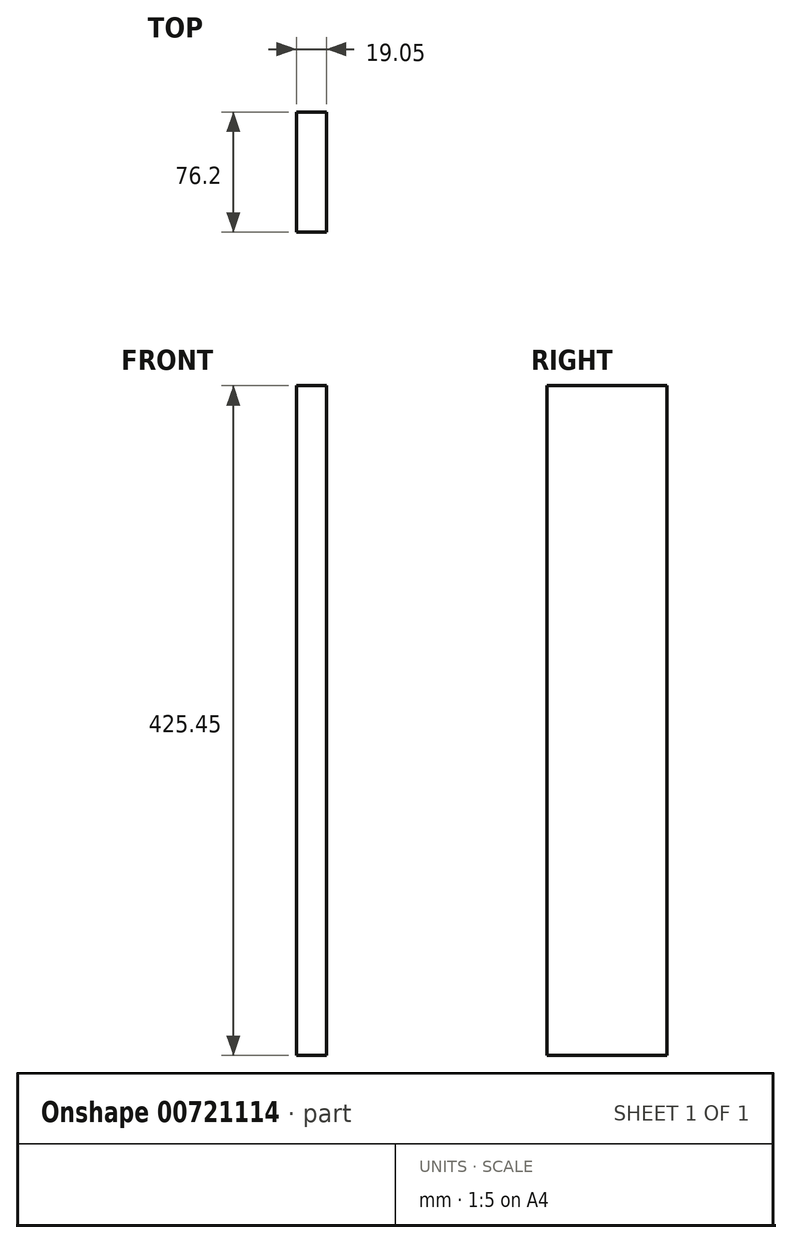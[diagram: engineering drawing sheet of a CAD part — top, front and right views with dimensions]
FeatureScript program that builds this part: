
annotation { "Feature Type Name" : "Feature", "Feature Type Description" : "" }
export const myFeature = defineFeature(function(context is Context, id is Id, definition is map)
    precondition{}
    {
        {
            var Q0;
            Q0=qCreatedBy(makeId("Top.planeOp"),FACE);
            var sketch = newSketch(context, id + "F0", { "sketchPlane" : qUnion([Q0])});
            skLineSegment(sketch, "E0.bottom", {"start": v(38.1, 38.1) * mm, "end": v(-38.1, 38.1) * mm});
            skLineSegment(sketch, "E0.top", {"start": v(38.1, -38.1) * mm, "end": v(-38.1, -38.1) * mm});
            skLineSegment(sketch, "E0.left", {"start": v(38.1, 38.1) * mm, "end": v(38.1, -38.1) * mm});
            skLineSegment(sketch, "E0.right", {"start": v(-38.1, 38.1) * mm, "end": v(-38.1, -38.1) * mm});
            skPoint(sketch, "E0.middle", {"position": v(0, 0) * mm});
            skLineSegment(sketch, "E1", {"start": v(-38.1, 38.1) * mm, "end": v(-19.05, 38.1) * mm});
            skLineSegment(sketch, "E2", {"start": v(-19.05, 38.1) * mm, "end": v(-19.05, -38.1) * mm});
            skLineSegment(sketch, "E3", {"start": v(38.1, -38.1) * mm, "end": v(38.1, -19.05) * mm});
            skLineSegment(sketch, "E4", {"start": v(38.1, -19.05) * mm, "end": v(-19.05, -19.05) * mm});
            skSolve(sketch);
        }
        {
            var Q0;
            {var subQ3=sQuery(id+"F0.wireOp",EDGE,"E0.right");Q0=makeQuery(id+"F0.imprint","IMPRINT",FACE,{"disambiguationData":[TD([[makeQuery(id+"F0.imprint","IMPRINT",EDGE,{"derivedFrom":subQ3}),1.0]])]});}
            var Q1;
            {var subQ0=sQuery(id+"F0.wireOp",EDGE,"E3");Q1=makeQuery(id+"F0.imprint","IMPRINT",FACE,{"disambiguationData":[TD([[makeQuery(id+"F0.imprint","IMPRINT",EDGE,{"derivedFrom":subQ0}),1.0]])]});}
            extrude(context, id + "F1", {"entities" : qUnion([Q0, Q1]), "depth" : 425.45 * mm, "offsetDistance" : 25.4 * mm});
        }
    });
